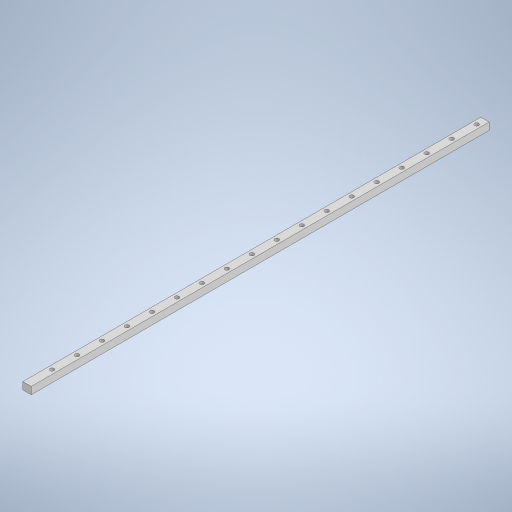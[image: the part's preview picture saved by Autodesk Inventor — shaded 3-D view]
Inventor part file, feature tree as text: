
AUTODESK INVENTOR PART (.ipt)
format: ipt  version: 2023 (Build 270158000, 158)  size: 285,696 bytes
history: native  units: mm
features: extrude x3, sketch x3, pattern_linear x1
ambient origin geometry x8: Origin, YZ Plane, XZ Plane, XY Plane, X Axis, Y Axis, Z Axis, Center Point
bodies: Solid1 (feature_tree)
feature tree (7):
  extrude  "Extrusion1"  Depth=17.5mm
  extrude  "Extrusion2"  Depth=1100.0mm
  extrude  "Extrusion3"  Depth=8.5mm TaperAngle=0.0deg
  pattern_linear  "Rectangular Pattern1"  Spacing1=9.5mm  [1 undecoded]
  sketch  "Sketch1"  dims[d0=20.0mm d1=17.5mm]
  sketch  "Sketch2"  dims[d2=1100.0mm d3=0.0mm d4=6.0mm]
  sketch  "Sketch3"  dims[d5=20.0mm d6=800.0mm d7=0.0mm d8=9.5mm d9=8.5mm d10=0.0mm d11=180.0mm d13=60.0mm]
note: 1 required parameter value undecoded (feature->parameter linkage not recoverable at this tier; creation-order binding heuristic only, values carry confidence <= 0.55)
